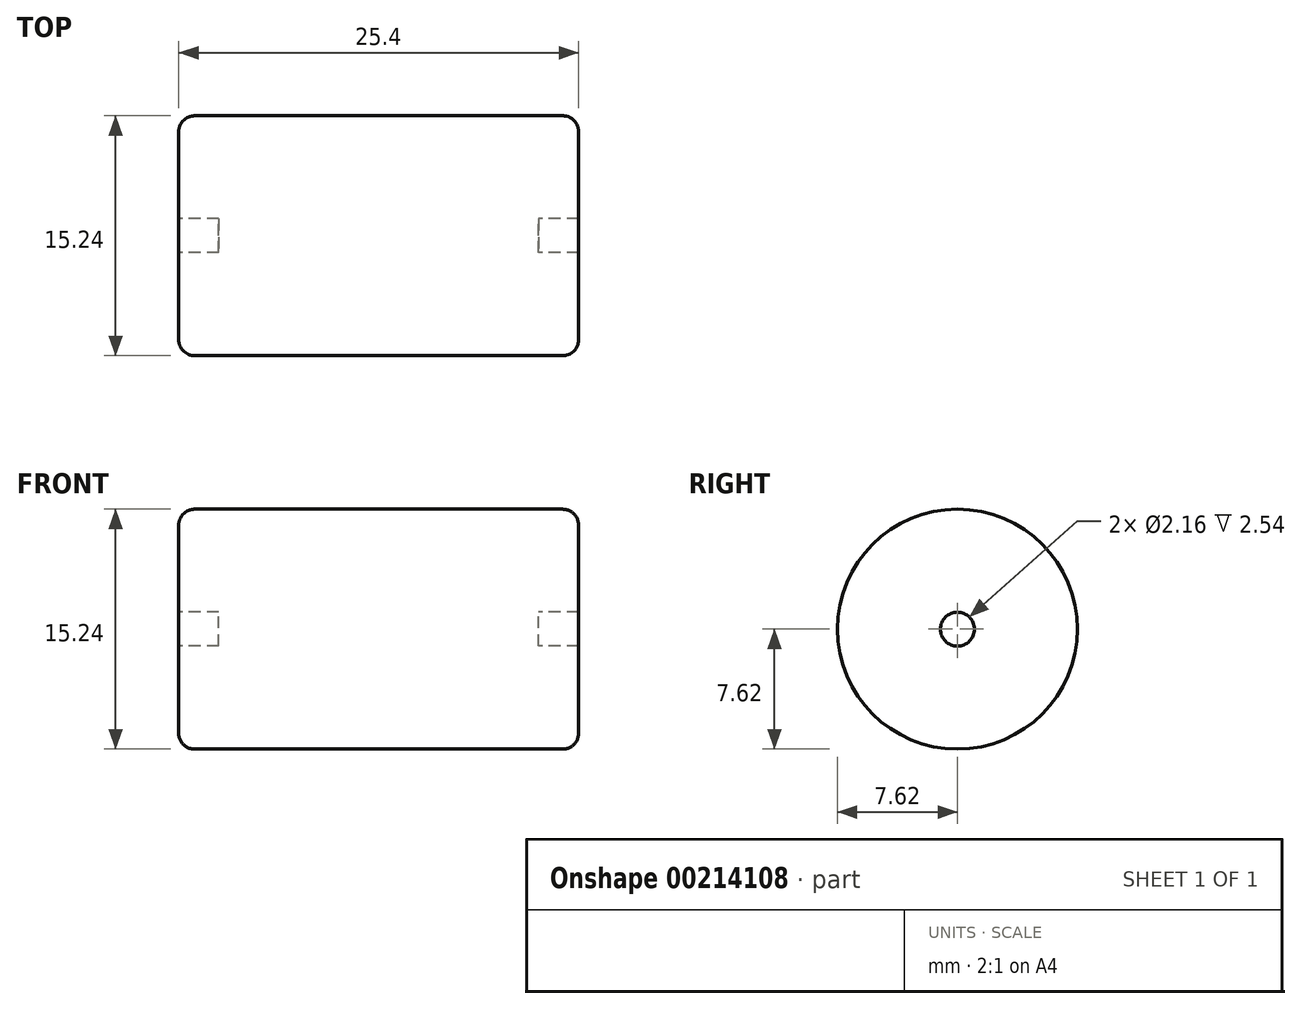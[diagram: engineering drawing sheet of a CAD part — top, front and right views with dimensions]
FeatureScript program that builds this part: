
annotation { "Feature Type Name" : "Feature", "Feature Type Description" : "" }
export const myFeature = defineFeature(function(context is Context, id is Id, definition is map)
    precondition{}
    {
        {
            var Q0;
            Q0=qCreatedBy(makeId("Right.planeOp"),FACE);
            var sketch = newSketch(context, id + "F0", { "sketchPlane" : qUnion([Q0])});
            skCircle(sketch, "E0", {"center": v(0, 0) * mm, "radius": 7.62 * mm});
            skCircle(sketch, "E1", {"center": v(0, 0) * mm, "radius": 1.08 * mm});
            skSolve(sketch);
        }
        {
            var Q0;
            Q0=makeQuery(id+"F0.imprint","IMPRINT",FACE,{"disambiguationData":[TD([[makeQuery(id+"F0.imprint","IMPRINT",EDGE,{"derivedFrom":sQuery(id+"F0.wireOp",EDGE,"E0")}),1.0]])]});
            extrude(context, id + "F1", {"entities" : qUnion([Q0]), "endBound" : BoundingType.SYMMETRIC, "depth" : 25.4 * mm});
        }
        {
            var Q0;
            Q0=makeQuery(id+"F0.imprint","IMPRINT",FACE,{"disambiguationData":[TD([[makeQuery(id+"F0.imprint","IMPRINT",EDGE,{"derivedFrom":sQuery(id+"F0.wireOp",EDGE,"E1")}),1.0]])]});
            extrude(context, id + "F2", {"entities" : qUnion([Q0]), "operationType" : NewBodyOperationType.ADD, "endBound" : BoundingType.SYMMETRIC, "depth" : 20.32 * mm});
        }
        {
            var Q0;
            Q0=makeQuery(id+"F1.opExtrude","CAP_EDGE",EDGE,{"disambiguationData":[OSD([sQuery(id+"F0.wireOp",EDGE,"E0")])],"isStart":false});
            var Q1;
            Q1=makeQuery(id+"F1.opExtrude","CAP_EDGE",EDGE,{"disambiguationData":[OSD([sQuery(id+"F0.wireOp",EDGE,"E0")])],"isStart":true});
            fillet(context, id + "F3", {"entities" : qUnion([Q0, Q1]), "radius" : 1.02 * mm, "tangentPropagation" : true, "allowEdgeOverflow" : false});
        }
    });
